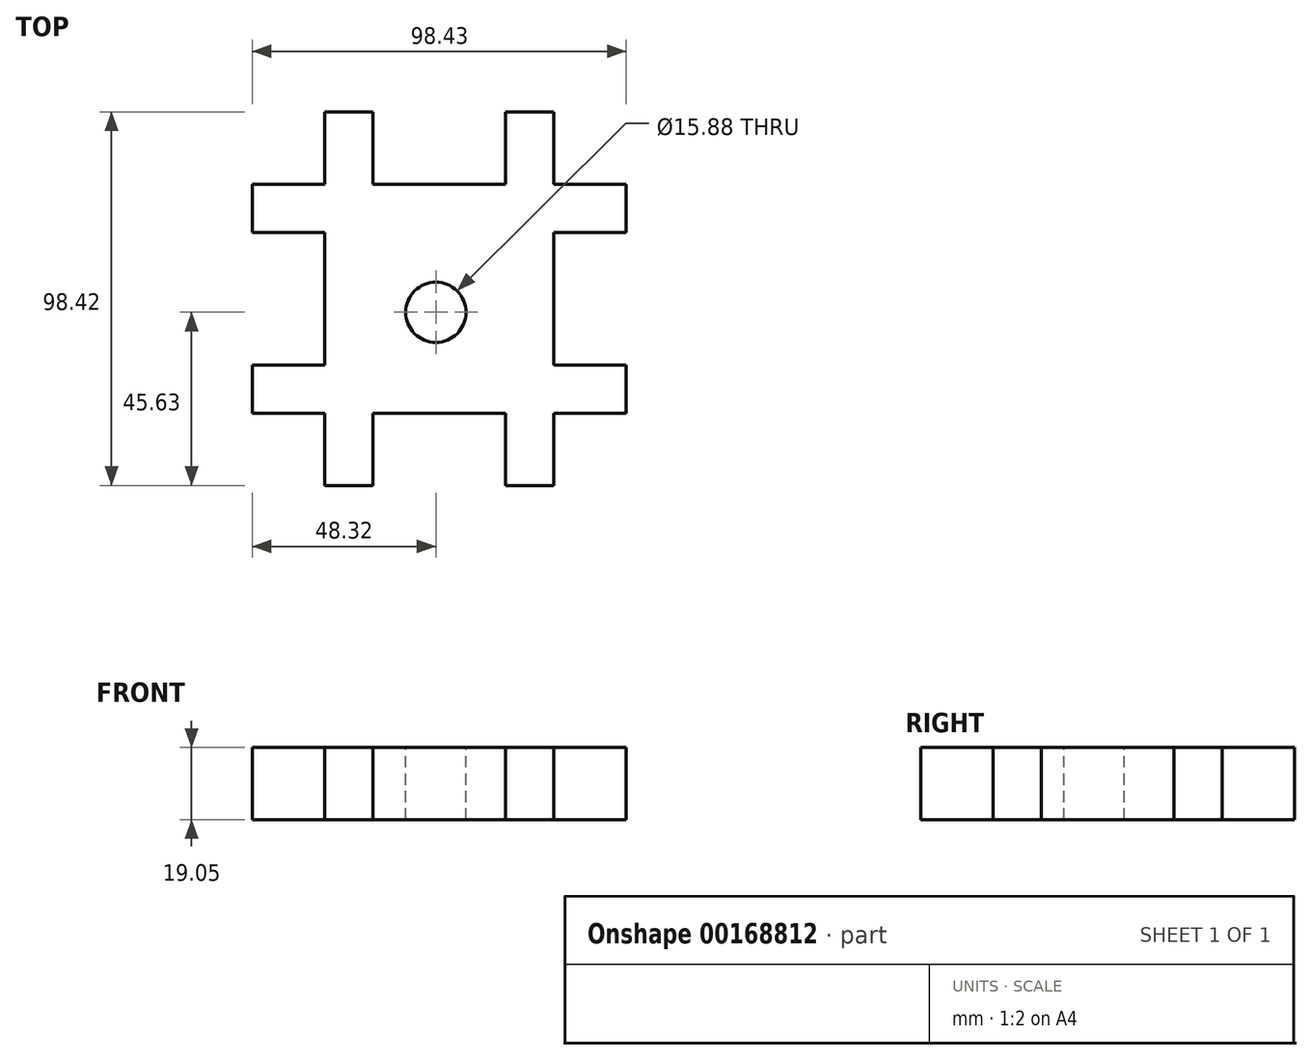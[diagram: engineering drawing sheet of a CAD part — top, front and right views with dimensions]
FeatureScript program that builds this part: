
annotation { "Feature Type Name" : "Feature", "Feature Type Description" : "" }
export const myFeature = defineFeature(function(context is Context, id is Id, definition is map)
    precondition{}
    {
        {
            var Q0;
            Q0=qCreatedBy(makeId("Top.planeOp"),FACE);
            var sketch = newSketch(context, id + "F0", { "sketchPlane" : qUnion([Q0])});
            skLineSegment(sketch, "E0.bottom", {"start": v(-48.32, 52.8) * mm, "end": v(50.1, 52.8) * mm});
            skLineSegment(sketch, "E0.top", {"start": v(-48.32, -45.63) * mm, "end": v(50.1, -45.63) * mm});
            skLineSegment(sketch, "E0.left", {"start": v(-48.32, 52.8) * mm, "end": v(-48.32, -45.63) * mm});
            skLineSegment(sketch, "E0.right", {"start": v(50.1, 52.8) * mm, "end": v(50.1, -45.63) * mm});
            skSolve(sketch);
        }
        {
            var Q0;
            Q0 = qSketchRegion(id + "F0", true);
            extrude(context, id + "F1", {"entities" : qUnion([Q0]), "depth" : 19.05 * mm});
        }
        {
            var Q0;
            Q0=makeQuery(id+"F1.opExtrude","CAP_FACE",FACE,{"disambiguationData":[OSD([sQuery(id+"F0.wireOp",EDGE,"E0.bottom"),sQuery(id+"F0.wireOp",EDGE,"E0.top"),sQuery(id+"F0.wireOp",EDGE,"E0.left"),sQuery(id+"F0.wireOp",EDGE,"E0.right")])],"isStart":false});
            var sketch = newSketch(context, id + "F2", { "sketchPlane" : qUnion([Q0])});
            skLineSegment(sketch, "E1", {"start": v(-29.27, 52.8) * mm, "end": v(-29.27, -45.63) * mm});
            skLineSegment(sketch, "E2", {"start": v(31.06, 52.8) * mm, "end": v(31.06, -45.63) * mm});
            skLineSegment(sketch, "E3", {"start": v(-48.32, 33.74) * mm, "end": v(50.1, 33.74) * mm});
            skLineSegment(sketch, "E4", {"start": v(-48.32, -26.58) * mm, "end": v(50.1, -26.58) * mm});
            skLineSegment(sketch, "E5", {"start": v(-16.57, 52.8) * mm, "end": v(-16.57, -45.63) * mm});
            skLineSegment(sketch, "E6", {"start": v(18.36, 52.8) * mm, "end": v(18.36, -45.63) * mm});
            skLineSegment(sketch, "E7", {"start": v(-48.32, 21.04) * mm, "end": v(50.1, 21.04) * mm});
            skLineSegment(sketch, "E8", {"start": v(-48.32, -13.88) * mm, "end": v(50.1, -13.88) * mm});
            skSolve(sketch);
        }
        {
            var Q0;
            {var subQ0=sQuery(id+"F2.wireOp",EDGE,"E1");var subQ1=makeQuery(id+"F1.opExtrude","CAP_EDGE",EDGE,{"disambiguationData":[OSD([sQuery(id+"F0.wireOp",EDGE,"E0.bottom")])],"isStart":false});var subQ2=makeQuery(id+"F2.imprint","INTERSECT",VERTEX,{"derivedFrom":[subQ1,subQ0]});Q0=makeQuery(id+"F2.imprint","IMPRINT",FACE,{"disambiguationData":[TD([[makeQuery(id+"F2.imprint","IMPRINT",EDGE,{"disambiguationData":[TD([[subQ2,-1.0]])],"derivedFrom":subQ0}),-1.0]])]});}
            var Q1;
            {var subQ0=sQuery(id+"F2.wireOp",EDGE,"E2");var subQ1=makeQuery(id+"F1.opExtrude","CAP_EDGE",EDGE,{"disambiguationData":[OSD([sQuery(id+"F0.wireOp",EDGE,"E0.bottom")])],"isStart":false});var subQ2=makeQuery(id+"F2.imprint","INTERSECT",VERTEX,{"derivedFrom":[subQ1,subQ0]});Q1=makeQuery(id+"F2.imprint","IMPRINT",FACE,{"disambiguationData":[TD([[makeQuery(id+"F2.imprint","IMPRINT",EDGE,{"disambiguationData":[TD([[subQ2,-1.0]])],"derivedFrom":subQ0}),1.0]])]});}
            var Q2;
            {var subQ0=sQuery(id+"F2.wireOp",EDGE,"E1");var subQ1=makeQuery(id+"F1.opExtrude","CAP_EDGE",EDGE,{"disambiguationData":[OSD([sQuery(id+"F0.wireOp",EDGE,"E0.top")])],"isStart":false});var subQ2=makeQuery(id+"F2.imprint","INTERSECT",VERTEX,{"derivedFrom":[subQ1,subQ0]});Q2=makeQuery(id+"F2.imprint","IMPRINT",FACE,{"disambiguationData":[TD([[makeQuery(id+"F2.imprint","IMPRINT",EDGE,{"disambiguationData":[TD([[subQ2,1.0]])],"derivedFrom":subQ0}),-1.0]])]});}
            var Q3;
            {var subQ0=sQuery(id+"F2.wireOp",EDGE,"E2");var subQ1=makeQuery(id+"F1.opExtrude","CAP_EDGE",EDGE,{"disambiguationData":[OSD([sQuery(id+"F0.wireOp",EDGE,"E0.top")])],"isStart":false});var subQ2=makeQuery(id+"F2.imprint","INTERSECT",VERTEX,{"derivedFrom":[subQ1,subQ0]});Q3=makeQuery(id+"F2.imprint","IMPRINT",FACE,{"disambiguationData":[TD([[makeQuery(id+"F2.imprint","IMPRINT",EDGE,{"disambiguationData":[TD([[subQ2,1.0]])],"derivedFrom":subQ0}),1.0]])]});}
            var Q4;
            {var subQ0=sQuery(id+"F2.wireOp",EDGE,"E7");var subQ1=sQuery(id+"F2.wireOp",EDGE,"E2");var subQ2=makeQuery(id+"F2.imprint","INTERSECT",VERTEX,{"derivedFrom":[subQ1,subQ0]});Q4=makeQuery(id+"F2.imprint","IMPRINT",FACE,{"disambiguationData":[TD([[makeQuery(id+"F2.imprint","IMPRINT",EDGE,{"disambiguationData":[TD([[subQ2,-1.0]])],"derivedFrom":subQ1}),1.0]])]});}
            var Q5;
            {var subQ0=sQuery(id+"F2.wireOp",EDGE,"E7");var subQ1=sQuery(id+"F2.wireOp",EDGE,"E1");var subQ2=makeQuery(id+"F2.imprint","INTERSECT",VERTEX,{"derivedFrom":[subQ1,subQ0]});Q5=makeQuery(id+"F2.imprint","IMPRINT",FACE,{"disambiguationData":[TD([[makeQuery(id+"F2.imprint","IMPRINT",EDGE,{"disambiguationData":[TD([[subQ2,-1.0]])],"derivedFrom":subQ1}),-1.0]])]});}
            var Q6;
            {var subQ0=sQuery(id+"F2.wireOp",EDGE,"E5");var subQ1=sQuery(id+"F2.wireOp",EDGE,"E3");var subQ2=makeQuery(id+"F2.imprint","INTERSECT",VERTEX,{"derivedFrom":[subQ1,subQ0]});Q6=makeQuery(id+"F2.imprint","IMPRINT",FACE,{"disambiguationData":[TD([[makeQuery(id+"F2.imprint","IMPRINT",EDGE,{"disambiguationData":[TD([[subQ2,-1.0]])],"derivedFrom":subQ1}),1.0]])]});}
            var Q7;
            {var subQ0=sQuery(id+"F2.wireOp",EDGE,"E5");var subQ1=sQuery(id+"F2.wireOp",EDGE,"E4");var subQ2=makeQuery(id+"F2.imprint","INTERSECT",VERTEX,{"derivedFrom":[subQ1,subQ0]});Q7=makeQuery(id+"F2.imprint","IMPRINT",FACE,{"disambiguationData":[TD([[makeQuery(id+"F2.imprint","IMPRINT",EDGE,{"disambiguationData":[TD([[subQ2,-1.0]])],"derivedFrom":subQ1}),-1.0]])]});}
            extrude(context, id + "F3", {"entities" : qUnion([Q0, Q1, Q2, Q3, Q4, Q5, Q6, Q7]), "operationType" : NewBodyOperationType.REMOVE, "endBound" : BoundingType.THROUGH_ALL, "oppositeDirection" : true, "depth" : 25.4 * mm});
        }
        {
            var Q0;
            Q0=makeQuery(id+"F1.opExtrude","CAP_FACE",FACE,{"disambiguationData":[OSD([sQuery(id+"F0.wireOp",EDGE,"E0.bottom"),sQuery(id+"F0.wireOp",EDGE,"E0.top"),sQuery(id+"F0.wireOp",EDGE,"E0.left"),sQuery(id+"F0.wireOp",EDGE,"E0.right")])],"isStart":false});
            var sketch = newSketch(context, id + "F4", { "sketchPlane" : qUnion([Q0])});
            skLineSegment(sketch, "E9", {"start": v(0, 33.74) * mm, "end": v(0, -26.58) * mm, "construction": true});
            skCircle(sketch, "E10", {"center": v(0, 0) * mm, "radius": 7.94 * mm});
            skSolve(sketch);
        }
        {
            var Q0;
            Q0 = qSketchRegion(id + "F4", true);
            extrude(context, id + "F5", {"entities" : qUnion([Q0]), "operationType" : NewBodyOperationType.REMOVE, "endBound" : BoundingType.THROUGH_ALL, "oppositeDirection" : true, "depth" : 25.4 * mm});
        }
    });
